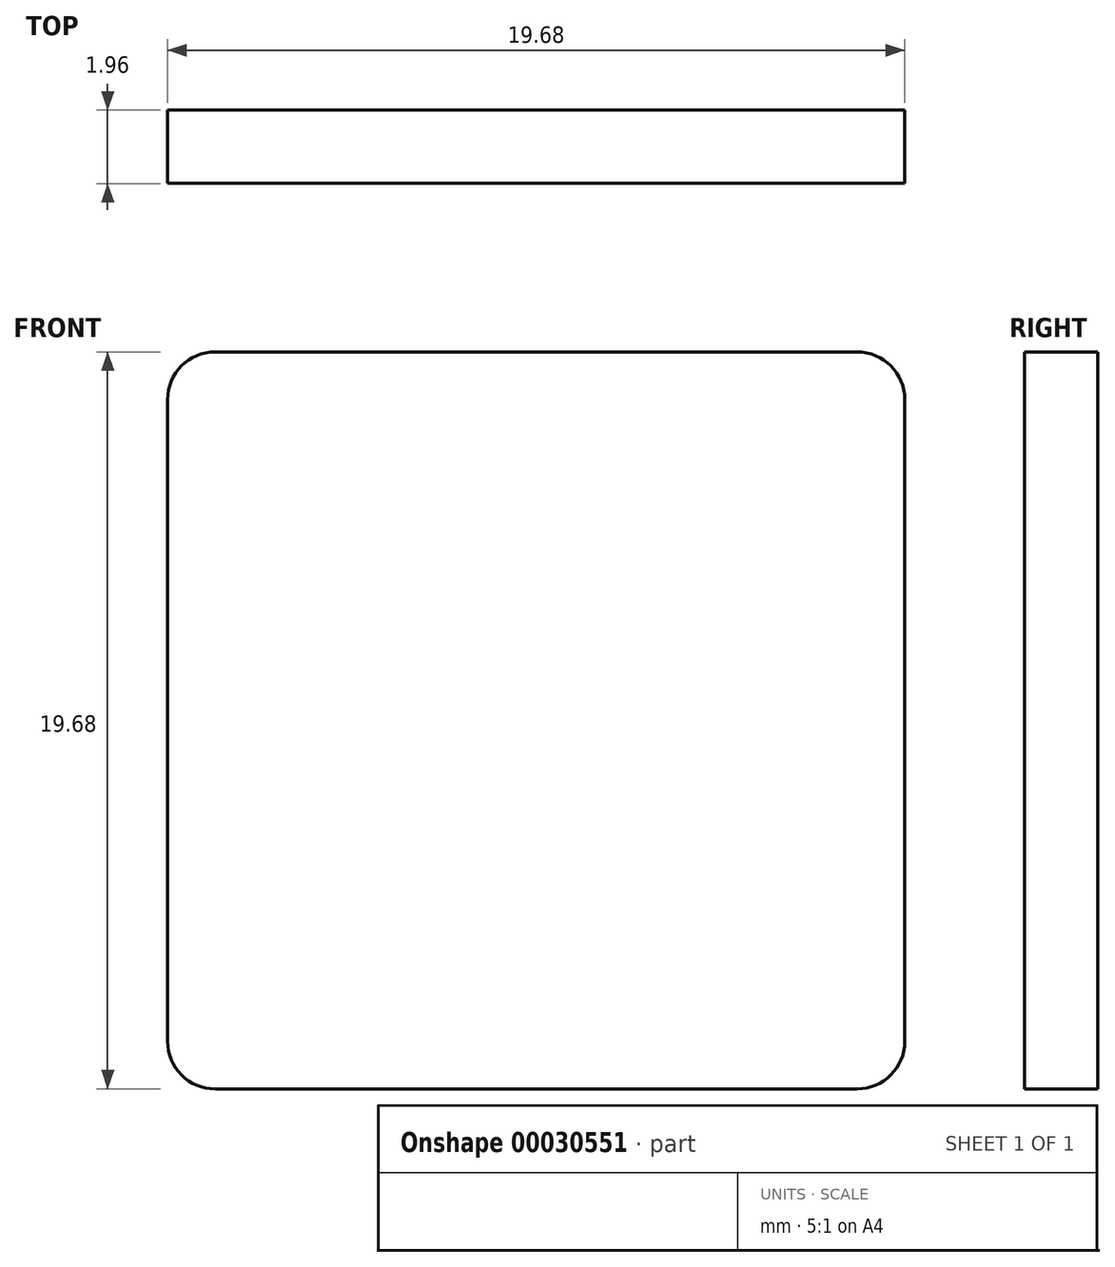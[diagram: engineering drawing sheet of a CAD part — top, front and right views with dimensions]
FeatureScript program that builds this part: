
annotation { "Feature Type Name" : "Feature", "Feature Type Description" : "" }
export const myFeature = defineFeature(function(context is Context, id is Id, definition is map)
    precondition{}
    {
        {
            var Q0;
            Q0=qCreatedBy(makeId("Front.planeOp"),FACE);
            var sketch = newSketch(context, id + "F0", { "sketchPlane" : qUnion([Q0])});
            skLineSegment(sketch, "E0.rect.bottom", {"start": v(9.84, 9.84) * mm, "end": v(-9.84, 9.84) * mm});
            skLineSegment(sketch, "E0.rect.top", {"start": v(9.84, -9.84) * mm, "end": v(-9.84, -9.84) * mm});
            skLineSegment(sketch, "E0.rect.left", {"start": v(9.84, 9.84) * mm, "end": v(9.84, -9.84) * mm});
            skLineSegment(sketch, "E0.rect.right", {"start": v(-9.84, 9.84) * mm, "end": v(-9.84, -9.84) * mm});
            skPoint(sketch, "E0.rect.middle", {"position": v(0, 0) * mm});
            skSolve(sketch);
        }
        {
            var Q0;
            Q0=makeQuery(id+"F0.imprint","IMPRINT",FACE,{"disambiguationData":[TD([[makeQuery(id+"F0.imprint","IMPRINT",EDGE,{"derivedFrom":sQuery(id+"F0.wireOp",EDGE,"E0.rect.bottom")}),1.0]])]});
            extrude(context, id + "F1", {"entities" : qUnion([Q0]), "depth" : 1.96 * mm});
        }
        {
            var Q0;
            Q0=makeQuery(id+"F1.opExtrude","SWEPT_EDGE",EDGE,{"disambiguationData":[OSD([sQuery(id+"F0.wireOp",EDGE,"E0.rect.bottom"),sQuery(id+"F0.wireOp",EDGE,"E0.rect.left")])]});
            var Q1;
            Q1=makeQuery(id+"F1.opExtrude","SWEPT_EDGE",EDGE,{"disambiguationData":[OSD([sQuery(id+"F0.wireOp",EDGE,"E0.rect.top"),sQuery(id+"F0.wireOp",EDGE,"E0.rect.left")])]});
            var Q2;
            Q2=makeQuery(id+"F1.opExtrude","SWEPT_EDGE",EDGE,{"disambiguationData":[OSD([sQuery(id+"F0.wireOp",EDGE,"E0.rect.bottom"),sQuery(id+"F0.wireOp",EDGE,"E0.rect.right")])]});
            var Q3;
            Q3=makeQuery(id+"F1.opExtrude","SWEPT_EDGE",EDGE,{"disambiguationData":[OSD([sQuery(id+"F0.wireOp",EDGE,"E0.rect.top"),sQuery(id+"F0.wireOp",EDGE,"E0.rect.right")])]});
            fillet(context, id + "F2", {"entities" : qUnion([Q0, Q1, Q2, Q3]), "radius" : 1.27 * mm, "tangentPropagation" : true, "allowEdgeOverflow" : false});
        }
    });
